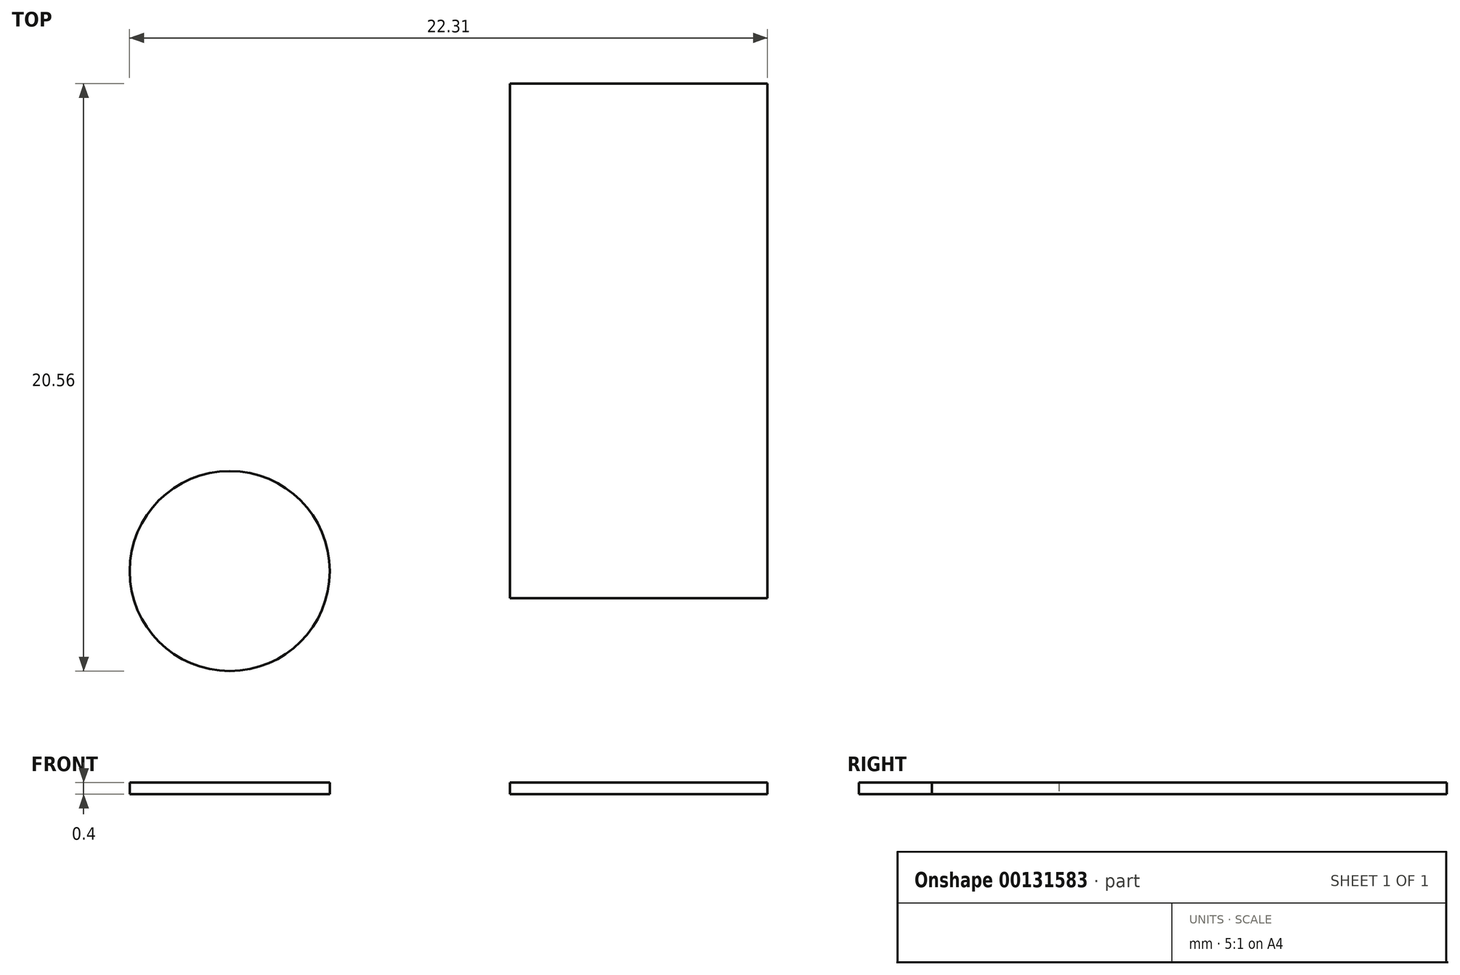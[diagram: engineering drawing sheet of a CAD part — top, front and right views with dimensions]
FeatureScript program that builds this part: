
annotation { "Feature Type Name" : "Feature", "Feature Type Description" : "" }
export const myFeature = defineFeature(function(context is Context, id is Id, definition is map)
    precondition{}
    {
        {
            var Q0;
            Q0=qCreatedBy(makeId("Top.planeOp"),FACE);
            var sketch = newSketch(context, id + "F0", { "sketchPlane" : qUnion([Q0])});
            skCircle(sketch, "E0", {"center": v(-23.37, 19.1) * mm, "radius": 3.5 * mm});
            skLineSegment(sketch, "E1.bottom", {"start": v(-13.56, 36.17) * mm, "end": v(-4.56, 36.17) * mm});
            skLineSegment(sketch, "E1.top", {"start": v(-13.56, 18.17) * mm, "end": v(-4.56, 18.17) * mm});
            skLineSegment(sketch, "E1.left", {"start": v(-13.56, 36.17) * mm, "end": v(-13.56, 18.17) * mm});
            skLineSegment(sketch, "E1.right", {"start": v(-4.56, 36.17) * mm, "end": v(-4.56, 18.17) * mm});
            skCircle(sketch, "E2", {"center": v(33.08, 11.74) * mm, "radius": 12.55 * mm});
            skCircle(sketch, "E3", {"center": v(33.08, 11.74) * mm, "radius": 13.5 * mm});
            skLineSegment(sketch, "E4.bottom", {"start": v(44.08, 15.81) * mm, "end": v(47.08, 15.81) * mm});
            skLineSegment(sketch, "E4.top", {"start": v(44.08, 7.66) * mm, "end": v(47.08, 7.66) * mm});
            skPoint(sketch, "E5.visualSharp", {"position": v(47.08, 15.81) * mm});
            skPoint(sketch, "E6.visualSharp", {"position": v(47.08, 7.66) * mm});
            skPoint(sketch, "E7.visualSharp", {"position": v(44.08, 7.66) * mm});
            skPoint(sketch, "E8.visualSharp", {"position": v(44.08, 15.81) * mm});
            skLineSegment(sketch, "E9", {"start": v(47.08, 15.81) * mm, "end": v(47.08, 7.66) * mm});
            skLineSegment(sketch, "E10", {"start": v(44.08, 7.66) * mm, "end": v(44.08, 15.81) * mm});
            skCircle(sketch, "E11", {"center": v(12.46, 57.05) * mm, "radius": 12.25 * mm});
            skSolve(sketch);
        }
        {
            var Q0;
            Q0=makeQuery(id+"F0.imprint","IMPRINT",FACE,{"disambiguationData":[TD([[makeQuery(id+"F0.imprint","IMPRINT",EDGE,{"derivedFrom":sQuery(id+"F0.wireOp",EDGE,"E0")}),1.0]])]});
            extrude(context, id + "F1", {"entities" : qUnion([Q0]), "depth" : .4 * mm});
        }
        {
            var Q0;
            Q0=makeQuery(id+"F0.imprint","IMPRINT",FACE,{"disambiguationData":[TD([[makeQuery(id+"F0.imprint","IMPRINT",EDGE,{"derivedFrom":sQuery(id+"F0.wireOp",EDGE,"E1.bottom")}),-1.0]])]});
            extrude(context, id + "F2", {"entities" : qUnion([Q0]), "depth" : .4 * mm});
        }
    });
